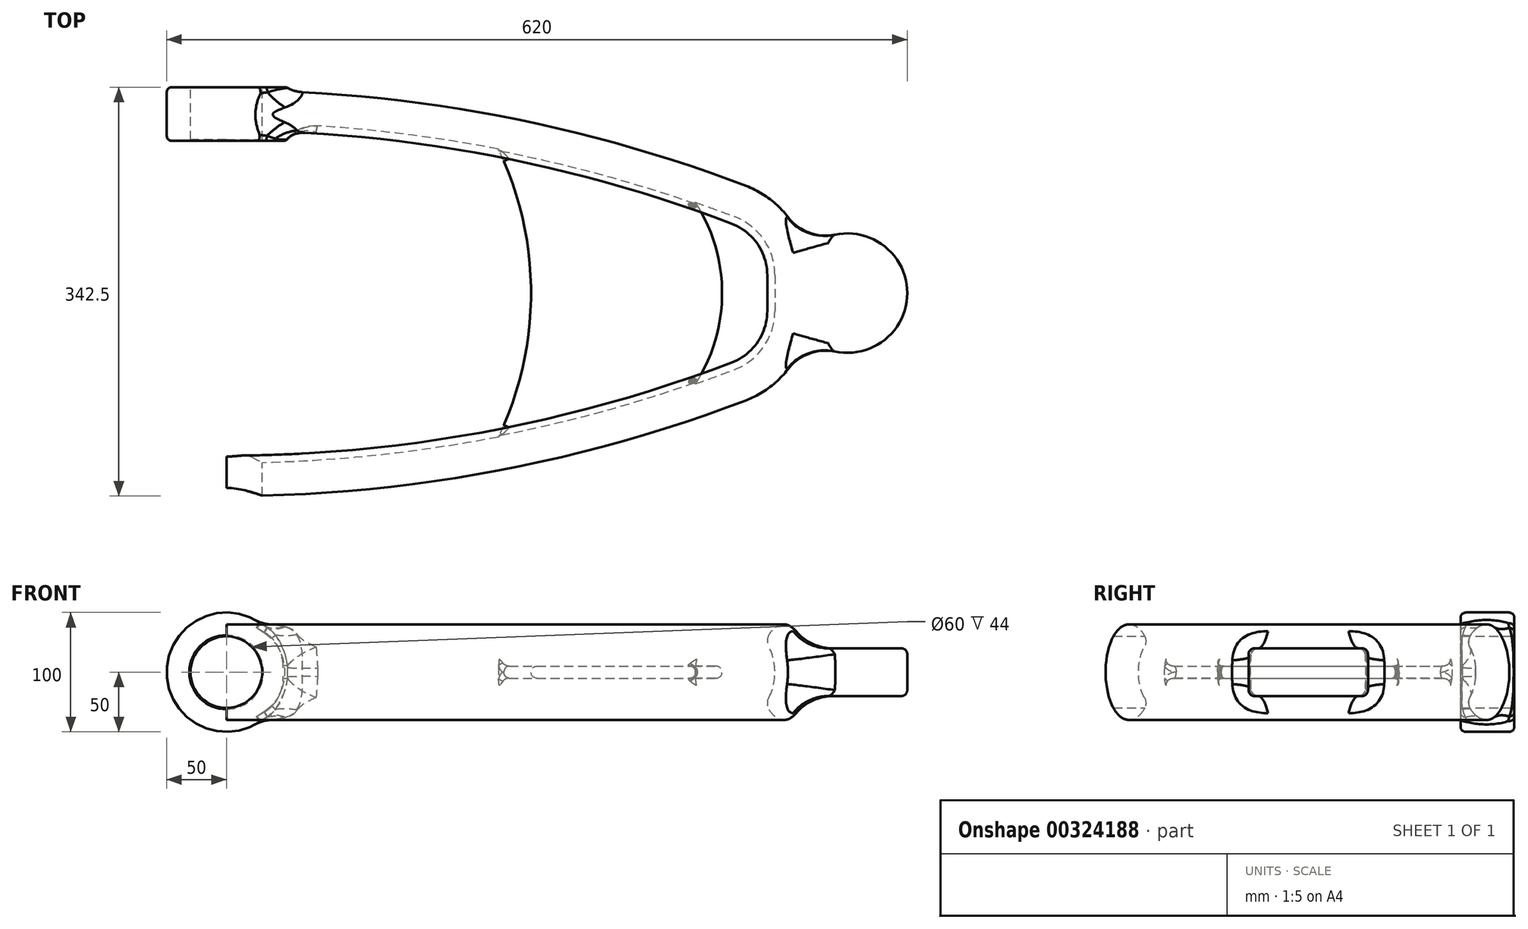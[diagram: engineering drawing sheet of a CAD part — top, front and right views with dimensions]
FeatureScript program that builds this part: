
annotation { "Feature Type Name" : "Feature", "Feature Type Description" : "" }
export const myFeature = defineFeature(function(context is Context, id is Id, definition is map)
    precondition{}
    {
        {
            var Q0;
            Q0=qCreatedBy(makeId("Top.planeOp"),FACE);
            var sketch = newSketch(context, id + "F0", { "sketchPlane" : qUnion([Q0])});
            skArc(sketch, "E0", {"start": v(28.07, 71.05) * mm, "mid": v(-182.36, 130.1) * mm, "end": v(-400, 150) * mm});
            skArc(sketch, "E1", {"start": v(66.66, 15) * mm, "mid": v(56.08, 49.03) * mm, "end": v(28.07, 71.05) * mm});
            skLineSegment(sketch, "E2", {"start": v(0, 0) * mm, "end": v(-439.5, 0) * mm, "construction": true});
            skLineSegment(sketch, "E3", {"start": v(-400, 150) * mm, "end": v(-513.06, 150) * mm, "construction": true});
            skLineSegment(sketch, "E4", {"start": v(-470.76, -150) * mm, "end": v(-400, -150) * mm, "construction": true});
            skArc(sketch, "E5", {"start": v(-400, -150) * mm, "mid": v(-182.36, -130.1) * mm, "end": v(28.07, -71.05) * mm});
            skArc(sketch, "E6", {"start": v(28.07, -71.05) * mm, "mid": v(56.08, -49.03) * mm, "end": v(66.66, -15) * mm});
            skLineSegment(sketch, "E7", {"start": v(66.66, 15) * mm, "end": v(66.66, -15) * mm});
            skLineSegment(sketch, "E8", {"start": v(66.66, 0) * mm, "end": v(0, 0) * mm});
            skSolve(sketch);
        }
        {
            var Q0;
            Q0=qCreatedBy(makeId("Right.planeOp"),FACE);
            var Q1;
            Q1=sQuery(id+"F0.wireOp",VERTEX,"E3.start");
            cPlane(context, id + "F1", {"entities" : qUnion([Q0, Q1]), "cplaneType" : CPlaneType.PLANE_POINT, "offset" : 25 * mm, "width" : 150 * mm, "height" : 150 * mm});
        }
        {
            var Q0;
            Q0=qCreatedBy(id+"F1.planeOp",FACE);
            var sketch = newSketch(context, id + "F2", { "sketchPlane" : qUnion([Q0])});
            skEllipse(sketch, "E9", {"center": v(150, 0) * mm, "majorRadius": 40 * mm, "minorRadius": 20 * mm, "majorAxis": v(0, 1)});
            skSolve(sketch);
        }
        {
            var Q0;
            Q0=makeQuery(id+"F2.imprint","IMPRINT",FACE,{"disambiguationData":[TD([[makeQuery(id+"F2.imprint","IMPRINT",EDGE,{"derivedFrom":sQuery(id+"F2.wireOp",EDGE,"E9")}),1.0]])]});
            var Q1;
            Q1=sQuery(id+"F0.wireOp",EDGE,"E0");
            var Q2;
            Q2=sQuery(id+"F0.wireOp",EDGE,"E1");
            var Q3;
            Q3=sQuery(id+"F0.wireOp",EDGE,"E7");
            var Q4;
            Q4=sQuery(id+"F0.wireOp",EDGE,"E6");
            var Q5;
            Q5=sQuery(id+"F0.wireOp",EDGE,"E5");
            sweep(context, id + "F3", {"profiles" : qUnion([Q0]), "path" : qUnion([Q1, Q2, Q3, Q4, Q5])});
        }
        {
            var Q0;
            Q0=qCreatedBy(id+"F1.planeOp",FACE);
            var sketch = newSketch(context, id + "F4", { "sketchPlane" : qUnion([Q0])});
            skEllipse(sketch, "E10", {"center": v(125, 0) * mm, "majorRadius": 30 * mm, "minorRadius": 17.5 * mm, "majorAxis": v(0, -1)});
            skSolve(sketch);
        }
        {
            var Q0;
            Q0=makeQuery(id+"F4.imprint","IMPRINT",FACE,{"disambiguationData":[TD([[makeQuery(id+"F4.imprint","IMPRINT",EDGE,{"derivedFrom":sQuery(id+"F4.wireOp",EDGE,"E10")}),1.0]])]});
            var Q1;
            Q1=sQuery(id+"F0.wireOp",EDGE,"E0");
            var Q2;
            Q2=sQuery(id+"F0.wireOp",EDGE,"E1");
            var Q3;
            Q3=sQuery(id+"F0.wireOp",EDGE,"E7");
            var Q4;
            Q4=sQuery(id+"F0.wireOp",EDGE,"E6");
            var Q5;
            Q5=sQuery(id+"F0.wireOp",EDGE,"E5");
            sweep(context, id + "F5", {"operationType" : NewBodyOperationType.REMOVE, "profiles" : qUnion([Q0]), "path" : qUnion([Q1, Q2, Q3, Q4, Q5])});
        }
        {
            var Q0;
            {var subQ0=sQuery(id+"F0.wireOp",EDGE,"E0");Q0=makeQuery(id+"F5.boolean.opBoolean","INTERSECT",EDGE,{"disambiguationData":[OD(0.0)],"derivedFrom":[makeQuery(id+"F3.opSweep","SWEPT_FACE",FACE,{"disambiguationData":[OSD([subQ0,sQuery(id+"F2.wireOp",EDGE,"E9")])]}),makeQuery(id+"F5.opSweep","SWEPT_FACE",FACE,{"disambiguationData":[OSD([subQ0,sQuery(id+"F4.wireOp",EDGE,"E10")])]})]});}
            var Q1;
            {var subQ0=sQuery(id+"F0.wireOp",EDGE,"E0");Q1=makeQuery(id+"F5.boolean.opBoolean","INTERSECT",EDGE,{"disambiguationData":[OD(1.0)],"derivedFrom":[makeQuery(id+"F3.opSweep","SWEPT_FACE",FACE,{"disambiguationData":[OSD([subQ0,sQuery(id+"F2.wireOp",EDGE,"E9")])]}),makeQuery(id+"F5.opSweep","SWEPT_FACE",FACE,{"disambiguationData":[OSD([subQ0,sQuery(id+"F4.wireOp",EDGE,"E10")])]})]});}
            fillet(context, id + "F6", {"entities" : qUnion([Q0, Q1]), "radius" : 10 * mm, "tangentPropagation" : true, "allowEdgeOverflow" : false});
        }
        {
            var Q0;
            Q0=sQuery(id+"F2.wireOp",VERTEX,"E9.center");
            var Q1;
            Q1=qCreatedBy(makeId("Front.planeOp"),FACE);
            cPlane(context, id + "F7", {"entities" : qUnion([Q0, Q1]), "cplaneType" : CPlaneType.PLANE_POINT, "offset" : 25 * mm, "width" : 150 * mm, "height" : 150 * mm});
        }
        {
            var Q0;
            Q0=qCreatedBy(id+"F7.planeOp",FACE);
            var sketch = newSketch(context, id + "F8", { "sketchPlane" : qUnion([Q0])});
            skCircle(sketch, "E11", {"center": v(-400, 0) * mm, "radius": 50 * mm});
            skSolve(sketch);
        }
        {
            var Q0;
            Q0=makeQuery(id+"F8.imprint","IMPRINT",FACE,{"disambiguationData":[TD([[makeQuery(id+"F8.imprint","IMPRINT",EDGE,{"derivedFrom":sQuery(id+"F8.wireOp",EDGE,"E11")}),1.0]])]});
            extrude(context, id + "F9", {"entities" : qUnion([Q0]), "operationType" : NewBodyOperationType.ADD, "depth" : 45 * mm, "symmetric" : true});
        }
        {
            var Q0;
            Q0=makeQuery(id+"F9.boolean.opBoolean","INTERSECT",EDGE,{"derivedFrom":[makeQuery(id+"F3.opSweep","SWEPT_FACE",FACE,{"disambiguationData":[OSD([sQuery(id+"F0.wireOp",EDGE,"E0"),sQuery(id+"F2.wireOp",EDGE,"E9")])]}),makeQuery(id+"F9.opExtrude","SWEPT_FACE",FACE,{"disambiguationData":[OSD([sQuery(id+"F8.wireOp",EDGE,"E11")])]})]});
            fillet(context, id + "F10", {"entities" : qUnion([Q0]), "radius" : 30 * mm, "tangentPropagation" : true, "allowEdgeOverflow" : false});
        }
        {
            var Q0;
            {var subQ0=sQuery(id+"F8.wireOp",EDGE,"E11");Q0=makeQuery(id+"F10.opFillet","BLEND_EDGE",EDGE,{"disambiguationData":[OD(0.0)],"blendedFrom":[makeQuery(id+"F9.boolean.opBoolean","INTERSECT",EDGE,{"derivedFrom":[makeQuery(id+"F3.opSweep","SWEPT_FACE",FACE,{"disambiguationData":[OSD([sQuery(id+"F0.wireOp",EDGE,"E0"),sQuery(id+"F2.wireOp",EDGE,"E9")])]}),makeQuery(id+"F9.opExtrude","SWEPT_FACE",FACE,{"disambiguationData":[OSD([subQ0])]})]}),makeQuery(id+"F9.opExtrude","CAP_FACE",FACE,{"disambiguationData":[OSD([subQ0])],"isStart":false})],"blendedInto":[makeQuery(id+"F9.opExtrude","CAP_FACE",FACE,{"disambiguationData":[OSD([subQ0])],"isStart":false})]});}
            var Q1;
            {var subQ0=sQuery(id+"F8.wireOp",EDGE,"E11");Q1=makeQuery(id+"F10.opFillet","BLEND_EDGE",EDGE,{"blendedFrom":[makeQuery(id+"F9.boolean.opBoolean","INTERSECT",EDGE,{"derivedFrom":[makeQuery(id+"F3.opSweep","SWEPT_FACE",FACE,{"disambiguationData":[OSD([sQuery(id+"F0.wireOp",EDGE,"E0"),sQuery(id+"F2.wireOp",EDGE,"E9")])]}),makeQuery(id+"F9.opExtrude","SWEPT_FACE",FACE,{"disambiguationData":[OSD([subQ0])]})]}),makeQuery(id+"F9.opExtrude","CAP_FACE",FACE,{"disambiguationData":[OSD([subQ0])],"isStart":true})],"blendedInto":[makeQuery(id+"F9.opExtrude","CAP_FACE",FACE,{"disambiguationData":[OSD([subQ0])],"isStart":true})]});}
            var Q2;
            Q2=makeQuery(id+"F9.opExtrude","CAP_EDGE",EDGE,{"disambiguationData":[OSD([sQuery(id+"F8.wireOp",EDGE,"E11")])],"isStart":true});
            var Q3;
            {var subQ0=sQuery(id+"F8.wireOp",EDGE,"E11");Q3=makeQuery(id+"F10.opFillet","BLEND_EDGE",EDGE,{"disambiguationData":[OD(3.0)],"blendedFrom":[makeQuery(id+"F9.boolean.opBoolean","INTERSECT",EDGE,{"derivedFrom":[makeQuery(id+"F3.opSweep","SWEPT_FACE",FACE,{"disambiguationData":[OSD([sQuery(id+"F0.wireOp",EDGE,"E0"),sQuery(id+"F2.wireOp",EDGE,"E9")])]}),makeQuery(id+"F9.opExtrude","SWEPT_FACE",FACE,{"disambiguationData":[OSD([subQ0])]})]}),makeQuery(id+"F9.opExtrude","CAP_FACE",FACE,{"disambiguationData":[OSD([subQ0])],"isStart":false})],"blendedInto":[makeQuery(id+"F9.opExtrude","CAP_FACE",FACE,{"disambiguationData":[OSD([subQ0])],"isStart":false})]});}
            var Q4;
            Q4=makeQuery(id+"F9.opExtrude","CAP_EDGE",EDGE,{"disambiguationData":[OSD([sQuery(id+"F8.wireOp",EDGE,"E11")])],"isStart":false});
            var Q5;
            {var subQ0=sQuery(id+"F8.wireOp",EDGE,"E11");Q5=makeQuery(id+"F10.opFillet","BLEND_EDGE",EDGE,{"disambiguationData":[OD(4.0)],"blendedFrom":[makeQuery(id+"F9.boolean.opBoolean","INTERSECT",EDGE,{"derivedFrom":[makeQuery(id+"F3.opSweep","SWEPT_FACE",FACE,{"disambiguationData":[OSD([sQuery(id+"F0.wireOp",EDGE,"E0"),sQuery(id+"F2.wireOp",EDGE,"E9")])]}),makeQuery(id+"F9.opExtrude","SWEPT_FACE",FACE,{"disambiguationData":[OSD([subQ0])]})]}),makeQuery(id+"F9.opExtrude","CAP_FACE",FACE,{"disambiguationData":[OSD([subQ0])],"isStart":false})],"blendedInto":[makeQuery(id+"F9.opExtrude","CAP_FACE",FACE,{"disambiguationData":[OSD([subQ0])],"isStart":false})]});}
            var Q6;
            {var subQ0=sQuery(id+"F8.wireOp",EDGE,"E11");Q6=makeQuery(id+"F10.opFillet","BLEND_EDGE",EDGE,{"disambiguationData":[OD(2.0)],"blendedFrom":[makeQuery(id+"F9.boolean.opBoolean","INTERSECT",EDGE,{"derivedFrom":[makeQuery(id+"F3.opSweep","SWEPT_FACE",FACE,{"disambiguationData":[OSD([sQuery(id+"F0.wireOp",EDGE,"E0"),sQuery(id+"F2.wireOp",EDGE,"E9")])]}),makeQuery(id+"F9.opExtrude","SWEPT_FACE",FACE,{"disambiguationData":[OSD([subQ0])]})]}),makeQuery(id+"F9.opExtrude","CAP_FACE",FACE,{"disambiguationData":[OSD([subQ0])],"isStart":false})],"blendedInto":[makeQuery(id+"F9.opExtrude","CAP_FACE",FACE,{"disambiguationData":[OSD([subQ0])],"isStart":false})]});}
            fillet(context, id + "F11", {"entities" : qUnion([Q0, Q1, Q2, Q3, Q4, Q5, Q6]), "radius" : 5 * mm, "tangentPropagation" : true, "rho" : 0.5, "crossSection" : FilletCrossSection.CONIC, "allowEdgeOverflow" : false});
        }
        {
            var Q0;
            Q0=makeQuery(id+"F9.opExtrude","CAP_FACE",FACE,{"disambiguationData":[OSD([sQuery(id+"F8.wireOp",EDGE,"E11")])],"isStart":true});
            var sketch = newSketch(context, id + "F12", { "sketchPlane" : qUnion([Q0])});
            skCircle(sketch, "E12", {"center": v(400, 0) * mm, "radius": 30 * mm});
            skSolve(sketch);
        }
        {
            var Q0;
            Q0=makeQuery(id+"F12.imprint","IMPRINT",FACE,{"disambiguationData":[TD([[makeQuery(id+"F12.imprint","IMPRINT",EDGE,{"derivedFrom":sQuery(id+"F12.wireOp",EDGE,"E12")}),1.0]])]});
            extrude(context, id + "F13", {"entities" : qUnion([Q0]), "operationType" : NewBodyOperationType.REMOVE, "endBound" : BoundingType.THROUGH_ALL, "oppositeDirection" : true, "depth" : 25 * mm});
        }
        {
            var Q0;
            Q0=qCreatedBy(makeId("Top.planeOp"),FACE);
            var sketch = newSketch(context, id + "F14", { "sketchPlane" : qUnion([Q0])});
            skCircle(sketch, "E13", {"center": v(120, 0) * mm, "radius": 50 * mm});
            skSolve(sketch);
        }
        {
            var Q0;
            Q0=makeQuery(id+"F14.imprint","IMPRINT",FACE,{"disambiguationData":[TD([[makeQuery(id+"F14.imprint","IMPRINT",EDGE,{"derivedFrom":sQuery(id+"F14.wireOp",EDGE,"E13")}),1.0]])]});
            extrude(context, id + "F15", {"entities" : qUnion([Q0]), "operationType" : NewBodyOperationType.ADD, "depth" : 40 * mm, "symmetric" : true});
        }
        {
            var Q0;
            Q0=makeQuery(id+"F15.opExtrude","CAP_EDGE",EDGE,{"disambiguationData":[OSD([sQuery(id+"F14.wireOp",EDGE,"E13")])],"isStart":true});
            var Q1;
            Q1=makeQuery(id+"F15.opExtrude","CAP_EDGE",EDGE,{"disambiguationData":[OSD([sQuery(id+"F14.wireOp",EDGE,"E13")])],"isStart":false});
            fillet(context, id + "F16", {"entities" : qUnion([Q0, Q1]), "radius" : 5 * mm, "tangentPropagation" : true, "allowEdgeOverflow" : false});
        }
        {
            var Q0;
            Q0=makeQuery(id+"F15.boolean.opBoolean","INTERSECT",EDGE,{"derivedFrom":[makeQuery(id+"F3.opSweep","SWEPT_FACE",FACE,{"disambiguationData":[OSD([sQuery(id+"F0.wireOp",EDGE,"E7"),sQuery(id+"F2.wireOp",EDGE,"E9")])]}),makeQuery(id+"F15.opExtrude","CAP_FACE",FACE,{"disambiguationData":[OSD([sQuery(id+"F14.wireOp",EDGE,"E13")])],"isStart":true})]});
            fillet(context, id + "F17", {"entities" : qUnion([Q0]), "radius" : 40 * mm, "tangentPropagation" : true, "allowEdgeOverflow" : false});
        }
        {
            var Q0;
            Q0=makeQuery(id+"F13.boolean.opBoolean","COPY",EDGE,{"derivedFrom":makeQuery(id+"F13.opExtrude","CAP_EDGE",EDGE,{"disambiguationData":[OSD([sQuery(id+"F12.wireOp",EDGE,"E12")])],"isStart":true})});
            var Q1;
            Q1=makeQuery(id+"F13.boolean.opBoolean","INTERSECT",EDGE,{"derivedFrom":[makeQuery(id+"F9.opExtrude","CAP_FACE",FACE,{"disambiguationData":[OSD([sQuery(id+"F8.wireOp",EDGE,"E11")])],"isStart":false}),makeQuery(id+"F13.opExtrude","SWEPT_FACE",FACE,{"disambiguationData":[OSD([sQuery(id+"F12.wireOp",EDGE,"E12")])]})]});
            var Q2;
            Q2=makeQuery(id+"F13.boolean.opBoolean","INTERSECT",EDGE,{"derivedFrom":[makeQuery(id+"FcmCyu5l10xMOln_1.1.F9.opExtrude","CAP_FACE",FACE,{"disambiguationData":[OSD([sQuery(id+"F8.wireOp",EDGE,"E11")])],"isStart":false}),makeQuery(id+"F13.opExtrude","SWEPT_FACE",FACE,{"disambiguationData":[OSD([sQuery(id+"F12.wireOp",EDGE,"E12")])]})]});
            var Q3;
            Q3=makeQuery(id+"F13.boolean.opBoolean","INTERSECT",EDGE,{"derivedFrom":[makeQuery(id+"FcmCyu5l10xMOln_1.1.F9.opExtrude","CAP_FACE",FACE,{"disambiguationData":[OSD([sQuery(id+"F8.wireOp",EDGE,"E11")])],"isStart":true}),makeQuery(id+"F13.opExtrude","SWEPT_FACE",FACE,{"disambiguationData":[OSD([sQuery(id+"F12.wireOp",EDGE,"E12")])]})]});
            chamfer(context, id + "F18", {"entities" : qUnion([Q0, Q1, Q2, Q3]), "width" : 1 * mm, "tangentPropagation" : true});
        }
        {
            var Q0;
            Q0=qCreatedBy(makeId("Top.planeOp"),FACE);
            var sketch = newSketch(context, id + "F19", { "sketchPlane" : qUnion([Q0])});
            skArc(sketch, "E14", {"start": v(-182.51, -140) * mm, "mid": v(-145, 0) * mm, "end": v(-182.51, 140) * mm});
            skArc(sketch, "E15", {"start": v(-13.76, -85) * mm, "mid": v(15, 0) * mm, "end": v(-13.76, 85) * mm});
            skArc(sketch, "E16", {"start": v(-13.76, 85) * mm, "mid": v(-97.37, 114.84) * mm, "end": v(-182.51, 140) * mm});
            skArc(sketch, "E17", {"start": v(-182.51, -140) * mm, "mid": v(-97.37, -114.84) * mm, "end": v(-13.76, -85) * mm});
            skLineSegment(sketch, "E18", {"start": v(-425, 0) * mm, "end": v(-125, 0) * mm, "construction": true});
            skLineSegment(sketch, "E19", {"start": v(-125, 0) * mm, "end": v(0, 0) * mm, "construction": true});
            skLineSegment(sketch, "E20", {"start": v(-182.51, 140) * mm, "end": v(-425, 0) * mm, "construction": true});
            skLineSegment(sketch, "E21", {"start": v(-182.51, -140) * mm, "end": v(-425, 0) * mm, "construction": true});
            skSolve(sketch);
        }
        {
            var Q0;
            Q0=makeQuery(id+"F19.imprint","IMPRINT",FACE,{"disambiguationData":[TD([[makeQuery(id+"F19.imprint","IMPRINT",EDGE,{"derivedFrom":sQuery(id+"F19.wireOp",EDGE,"E14")}),-1.0]])]});
            extrude(context, id + "F20", {"entities" : qUnion([Q0]), "operationType" : NewBodyOperationType.ADD, "depth" : 10 * mm, "symmetric" : true});
        }
        {
            var Q0;
            Q0=makeQuery(id+"F20.boolean.opBoolean","INTERSECT",EDGE,{"derivedFrom":[makeQuery(id+"F5.boolean.opBoolean","COPY",FACE,{"derivedFrom":makeQuery(id+"F5.opSweep","SWEPT_FACE",FACE,{"disambiguationData":[OSD([sQuery(id+"F0.wireOp",EDGE,"E0"),sQuery(id+"F4.wireOp",EDGE,"E10")])]})}),makeQuery(id+"F20.opExtrude","CAP_FACE",FACE,{"disambiguationData":[OSD([sQuery(id+"F19.wireOp",EDGE,"E14"),sQuery(id+"F19.wireOp",EDGE,"E15"),sQuery(id+"F19.wireOp",EDGE,"E16"),sQuery(id+"F19.wireOp",EDGE,"E17")])],"isStart":false})]});
            var Q1;
            Q1=makeQuery(id+"F20.boolean.opBoolean","INTERSECT",EDGE,{"derivedFrom":[makeQuery(id+"F5.boolean.opBoolean","COPY",FACE,{"derivedFrom":makeQuery(id+"F5.opSweep","SWEPT_FACE",FACE,{"disambiguationData":[OSD([sQuery(id+"F0.wireOp",EDGE,"E5"),sQuery(id+"F4.wireOp",EDGE,"E10")])]})}),makeQuery(id+"F20.opExtrude","CAP_FACE",FACE,{"disambiguationData":[OSD([sQuery(id+"F19.wireOp",EDGE,"E14"),sQuery(id+"F19.wireOp",EDGE,"E15"),sQuery(id+"F19.wireOp",EDGE,"E16"),sQuery(id+"F19.wireOp",EDGE,"E17")])],"isStart":false})]});
            var Q2;
            Q2=makeQuery(id+"F20.boolean.opBoolean","INTERSECT",EDGE,{"derivedFrom":[makeQuery(id+"F5.boolean.opBoolean","COPY",FACE,{"derivedFrom":makeQuery(id+"F5.opSweep","SWEPT_FACE",FACE,{"disambiguationData":[OSD([sQuery(id+"F0.wireOp",EDGE,"E5"),sQuery(id+"F4.wireOp",EDGE,"E10")])]})}),makeQuery(id+"F20.opExtrude","CAP_FACE",FACE,{"disambiguationData":[OSD([sQuery(id+"F19.wireOp",EDGE,"E14"),sQuery(id+"F19.wireOp",EDGE,"E15"),sQuery(id+"F19.wireOp",EDGE,"E16"),sQuery(id+"F19.wireOp",EDGE,"E17")])],"isStart":true})]});
            var Q3;
            Q3=makeQuery(id+"F20.boolean.opBoolean","INTERSECT",EDGE,{"derivedFrom":[makeQuery(id+"F5.boolean.opBoolean","COPY",FACE,{"derivedFrom":makeQuery(id+"F5.opSweep","SWEPT_FACE",FACE,{"disambiguationData":[OSD([sQuery(id+"F0.wireOp",EDGE,"E0"),sQuery(id+"F4.wireOp",EDGE,"E10")])]})}),makeQuery(id+"F20.opExtrude","CAP_FACE",FACE,{"disambiguationData":[OSD([sQuery(id+"F19.wireOp",EDGE,"E14"),sQuery(id+"F19.wireOp",EDGE,"E15"),sQuery(id+"F19.wireOp",EDGE,"E16"),sQuery(id+"F19.wireOp",EDGE,"E17")])],"isStart":true})]});
            fillet(context, id + "F21", {"entities" : qUnion([Q0, Q1, Q2, Q3]), "radius" : 5 * mm, "tangentPropagation" : true, "allowEdgeOverflow" : false});
        }
        {
            var Q0;
            Q0=makeQuery(id+"F20.opExtrude","CAP_EDGE",EDGE,{"disambiguationData":[OSD([sQuery(id+"F19.wireOp",EDGE,"E14")])],"isStart":true});
            var Q1;
            Q1=makeQuery(id+"F20.opExtrude","CAP_EDGE",EDGE,{"disambiguationData":[OSD([sQuery(id+"F19.wireOp",EDGE,"E14")])],"isStart":false});
            var Q2;
            Q2=makeQuery(id+"F20.opExtrude","CAP_EDGE",EDGE,{"disambiguationData":[OSD([sQuery(id+"F19.wireOp",EDGE,"E15")])],"isStart":true});
            var Q3;
            Q3=makeQuery(id+"F20.opExtrude","CAP_EDGE",EDGE,{"disambiguationData":[OSD([sQuery(id+"F19.wireOp",EDGE,"E15")])],"isStart":false});
            fillet(context, id + "F22", {"entities" : qUnion([Q0, Q1, Q2, Q3]), "radius" : 5 * mm, "tangentPropagation" : true, "allowEdgeOverflow" : false});
        }
    });
